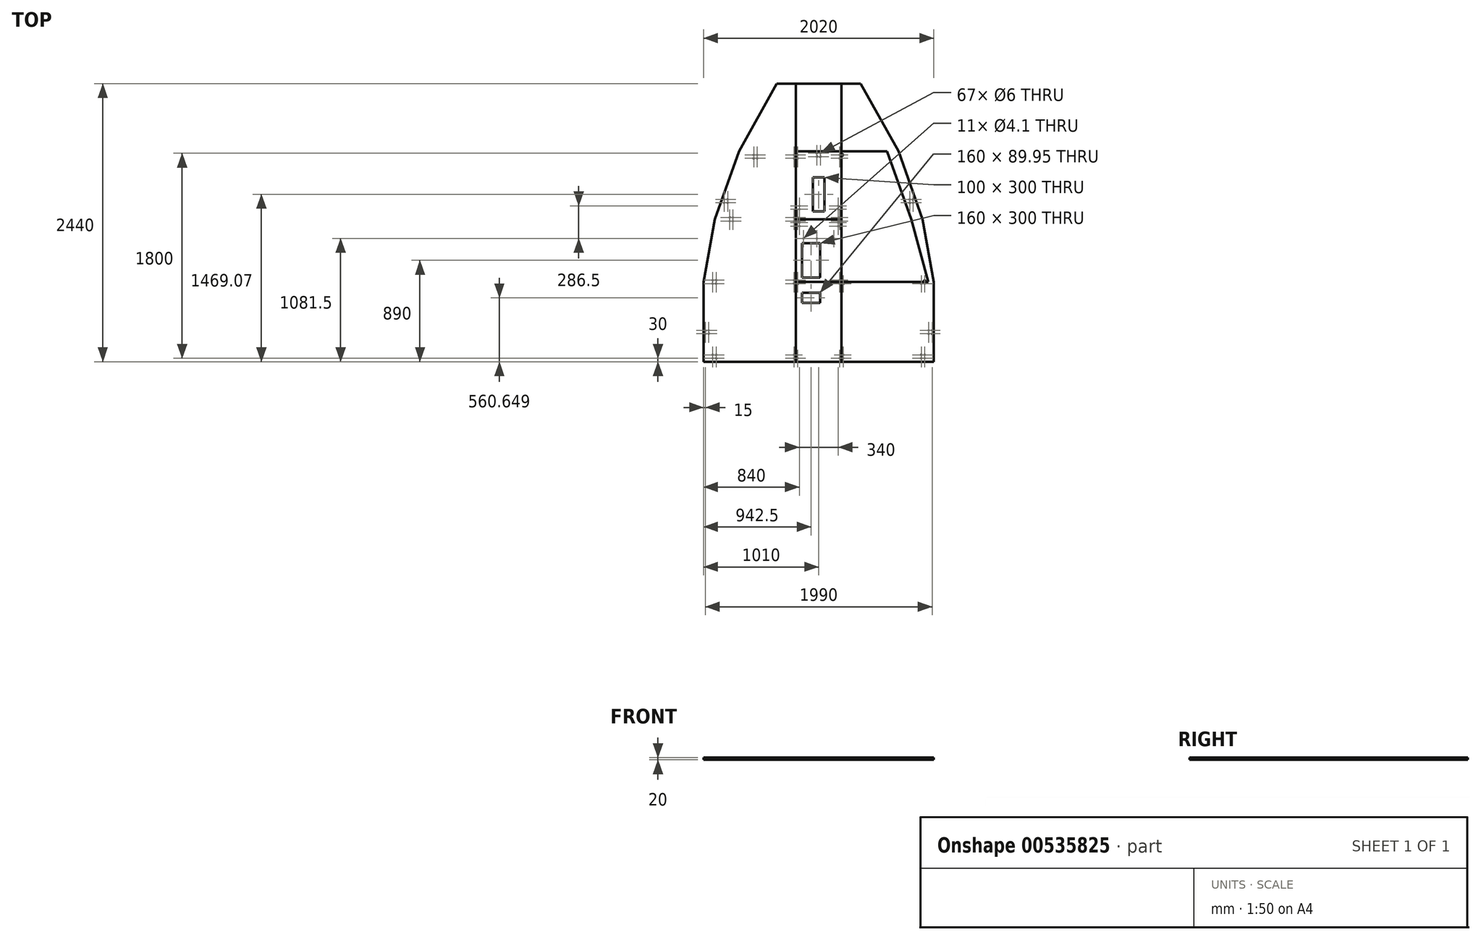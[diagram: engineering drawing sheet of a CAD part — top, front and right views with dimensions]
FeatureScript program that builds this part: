
annotation { "Feature Type Name" : "Feature", "Feature Type Description" : "" }
export const myFeature = defineFeature(function(context is Context, id is Id, definition is map)
    precondition{}
    {
        {
            var Q0;
            Q0=qCreatedBy(makeId("Top.planeOp"),FACE);
            var sketch = newSketch(context, id + "F0", { "sketchPlane" : qUnion([Q0])});
            skLineSegment(sketch, "E0.bottom", {"start": v(200, -350) * mm, "end": v(-200, -350) * mm});
            skLineSegment(sketch, "E0.top", {"start": v(200, 350) * mm, "end": v(-200, 350) * mm});
            skLineSegment(sketch, "E0.left", {"start": v(200, -350) * mm, "end": v(200, 350) * mm});
            skLineSegment(sketch, "E0.right", {"start": v(-200, -350) * mm, "end": v(-200, 350) * mm});
            skPoint(sketch, "E0.middle", {"position": v(0, 0) * mm});
            skCircle(sketch, "E1", {"center": v(185, 335) * mm, "radius": 3 * mm});
            skCircle(sketch, "E2", {"center": v(-185, 335) * mm, "radius": 3 * mm});
            skCircle(sketch, "E3", {"center": v(185, -320) * mm, "radius": 3 * mm});
            skCircle(sketch, "E4", {"center": v(-185, -320) * mm, "radius": 3 * mm});
            skLineSegment(sketch, "E5.bottom", {"start": v(12.5, 165.67) * mm, "end": v(-147.5, 165.67) * mm});
            skLineSegment(sketch, "E5.top", {"start": v(12.5, 255.63) * mm, "end": v(-147.5, 255.63) * mm});
            skLineSegment(sketch, "E5.left", {"start": v(12.5, 165.67) * mm, "end": v(12.5, 255.63) * mm});
            skLineSegment(sketch, "E5.right", {"start": v(-147.5, 165.67) * mm, "end": v(-147.5, 255.63) * mm});
            skPoint(sketch, "E5.middle", {"position": v(-67.5, 210.65) * mm});
            skSolve(sketch);
        }
        {
            var Q0;
            Q0=qSketchRegion(id+"F0",true);
            extrude(context, id + "F1", {"entities" : qUnion([Q0]), "depth" : 20 * mm});
        }
        {
            var Q0;
            Q0=qCreatedBy(makeId("Top.planeOp"),FACE);
            var sketch = newSketch(context, id + "F2", { "sketchPlane" : qUnion([Q0])});
            skLineSegment(sketch, "E6.top", {"start": v(-200, 900) * mm, "end": v(-812, 900) * mm});
            skLineSegment(sketch, "E6.left", {"start": v(-200, 350) * mm, "end": v(-200, 900) * mm});
            skPoint(sketch, "E6.middle", {"position": v(-506, 625) * mm});
            skLineSegment(sketch, "E7", {"start": v(-200, 350) * mm, "end": v(-960, 350) * mm});
            skLineSegment(sketch, "E8", {"start": v(-960, 350) * mm, "end": v(-812, 900) * mm});
            skCircle(sketch, "E9", {"center": v(-215, 885) * mm, "radius": 3 * mm});
            skCircle(sketch, "E10", {"center": v(-215, 365) * mm, "radius": 3 * mm});
            skCircle(sketch, "E11", {"center": v(-930, 365) * mm, "radius": 3 * mm});
            skCircle(sketch, "E12", {"center": v(-782, 885) * mm, "radius": 3 * mm});
            skLineSegment(sketch, "E13.left", {"start": v(-200, 900) * mm, "end": v(-200, 1495) * mm});
            skPoint(sketch, "E13.middle", {"position": v(-506, 1197.5) * mm});
            skLineSegment(sketch, "E14", {"start": v(-200, 1495) * mm, "end": v(-600, 1495) * mm});
            skLineSegment(sketch, "E15", {"start": v(-812, 900) * mm, "end": v(-600, 1495) * mm});
            skCircle(sketch, "E16", {"center": v(-215, 1465) * mm, "radius": 3 * mm});
            skCircle(sketch, "E17", {"center": v(-215, 915) * mm, "radius": 3 * mm});
            skCircle(sketch, "E18", {"center": v(-782, 915) * mm, "radius": 3 * mm});
            skCircle(sketch, "E19", {"center": v(-570, 1465) * mm, "radius": 3 * mm});
            skLineSegment(sketch, "E20", {"start": v(0, 1490.85) * mm, "end": v(0, 501.43) * mm, "construction": true});
            skCircle(sketch, "E21.MirrorC", {"center": v(215, 1465) * mm, "radius": 3 * mm});
            skCircle(sketch, "E22.MirrorC", {"center": v(930, 365) * mm, "radius": 3 * mm});
            skCircle(sketch, "E23.MirrorC", {"center": v(782, 885) * mm, "radius": 3 * mm});
            skCircle(sketch, "E24.MirrorC", {"center": v(782, 915) * mm, "radius": 3 * mm});
            skCircle(sketch, "E25.MirrorC", {"center": v(570, 1465) * mm, "radius": 3 * mm});
            skCircle(sketch, "E26.MirrorC", {"center": v(215, 885) * mm, "radius": 3 * mm});
            skCircle(sketch, "E27.MirrorC", {"center": v(215, 365) * mm, "radius": 3 * mm});
            skCircle(sketch, "E28.MirrorC", {"center": v(215, 915) * mm, "radius": 3 * mm});
            skLineSegment(sketch, "E29.MirrorCS", {"start": v(200, 1495) * mm, "end": v(600, 1495) * mm});
            skLineSegment(sketch, "E30.MirrorCS", {"start": v(960, 350) * mm, "end": v(812, 900) * mm});
            skLineSegment(sketch, "E31.MirrorCS", {"start": v(200, 900) * mm, "end": v(812, 900) * mm});
            skPoint(sketch, "E32.MirrorP", {"position": v(506, 1197.5) * mm});
            skLineSegment(sketch, "E33.MirrorCS", {"start": v(200, 350) * mm, "end": v(200, 900) * mm});
            skPoint(sketch, "E34.MirrorP", {"position": v(506, 625) * mm});
            skLineSegment(sketch, "E35.MirrorCS", {"start": v(200, 350) * mm, "end": v(960, 350) * mm});
            skLineSegment(sketch, "E36.MirrorCS", {"start": v(812, 900) * mm, "end": v(600, 1495) * mm});
            skLineSegment(sketch, "E37.MirrorCS", {"start": v(200, 900) * mm, "end": v(200, 1495) * mm});
            skCircle(sketch, "E38", {"center": v(-900, 365) * mm, "radius": 3 * mm});
            skCircle(sketch, "E39", {"center": v(-752, 885) * mm, "radius": 3 * mm});
            skCircle(sketch, "E40", {"center": v(-752, 915) * mm, "radius": 3 * mm});
            skCircle(sketch, "E41", {"center": v(-570, 1435) * mm, "radius": 3 * mm});
            skCircle(sketch, "E42", {"center": v(-540, 1465) * mm, "radius": 3 * mm});
            skCircle(sketch, "E43", {"center": v(-540, 1435) * mm, "radius": 3 * mm});
            skCircle(sketch, "E44", {"center": v(-215, 1435) * mm, "radius": 3 * mm});
            skCircle(sketch, "E45.MirrorC", {"center": v(215, 1435) * mm, "radius": 3 * mm});
            skCircle(sketch, "E46.MirrorC", {"center": v(540, 1465) * mm, "radius": 3 * mm});
            skCircle(sketch, "E47.MirrorC", {"center": v(540, 1435) * mm, "radius": 3 * mm});
            skCircle(sketch, "E48.MirrorC", {"center": v(570, 1435) * mm, "radius": 3 * mm});
            skCircle(sketch, "E49.MirrorC", {"center": v(752, 915) * mm, "radius": 3 * mm});
            skCircle(sketch, "E50.MirrorC", {"center": v(752, 885) * mm, "radius": 3 * mm});
            skCircle(sketch, "E51.MirrorC", {"center": v(900, 365) * mm, "radius": 3 * mm});
            skSolve(sketch);
        }
        {
            var Q0;
            Q0=makeQuery(id+"F2.imprint","IMPRINT",FACE,{"disambiguationData":[TD([[makeQuery(id+"F2.imprint","IMPRINT",EDGE,{"derivedFrom":sQuery(id+"F2.wireOp",EDGE,"E6.left")}),1.0]])]});
            var Q1;
            Q1=makeQuery(id+"F2.imprint","IMPRINT",FACE,{"disambiguationData":[TD([[makeQuery(id+"F2.imprint","IMPRINT",EDGE,{"derivedFrom":sQuery(id+"F2.wireOp",EDGE,"E22.MirrorC")}),1.0]])]});
            extrude(context, id + "F3", {"entities" : qUnion([Q0, Q1]), "depth" : 20 * mm});
        }
        {
            var Q0;
            Q0=makeQuery(id+"F2.imprint","IMPRINT",FACE,{"disambiguationData":[TD([[makeQuery(id+"F2.imprint","IMPRINT",EDGE,{"derivedFrom":sQuery(id+"F2.wireOp",EDGE,"E6.top")}),-1.0]])]});
            var Q1;
            Q1=makeQuery(id+"F2.imprint","IMPRINT",FACE,{"disambiguationData":[TD([[makeQuery(id+"F2.imprint","IMPRINT",EDGE,{"derivedFrom":sQuery(id+"F2.wireOp",EDGE,"E21.MirrorC")}),1.0]])]});
            extrude(context, id + "F4", {"entities" : qUnion([Q0, Q1]), "depth" : 20 * mm});
        }
        {
            var Q0;
            Q0=qCreatedBy(makeId("Top.planeOp"),FACE);
            var sketch = newSketch(context, id + "F5", { "sketchPlane" : qUnion([Q0])});
            skLineSegment(sketch, "E52.bottom", {"start": v(200, 900) * mm, "end": v(-200, 900) * mm});
            skLineSegment(sketch, "E52.top", {"start": v(200, 350) * mm, "end": v(-200, 350) * mm});
            skLineSegment(sketch, "E52.left", {"start": v(200, 900) * mm, "end": v(200, 350) * mm});
            skLineSegment(sketch, "E52.right", {"start": v(-200, 900) * mm, "end": v(-200, 350) * mm});
            skPoint(sketch, "E52.middle", {"position": v(0, 625) * mm});
            skCircle(sketch, "E53", {"center": v(-132.5, 731.5) * mm, "radius": 2.05 * mm});
            skCircle(sketch, "E54", {"center": v(-17.5, 731.5) * mm, "radius": 2.05 * mm});
            skCircle(sketch, "E55", {"center": v(132.5, 731.5) * mm, "radius": 2.05 * mm});
            skCircle(sketch, "E56", {"center": v(-185, 885) * mm, "radius": 3 * mm});
            skCircle(sketch, "E57", {"center": v(185, 885) * mm, "radius": 3 * mm});
            skCircle(sketch, "E58", {"center": v(-185, 365) * mm, "radius": 3 * mm});
            skCircle(sketch, "E59", {"center": v(185, 365) * mm, "radius": 3 * mm});
            skCircle(sketch, "E60", {"center": v(170, 870) * mm, "radius": 2.05 * mm});
            skCircle(sketch, "E61", {"center": v(170, 840) * mm, "radius": 2.05 * mm});
            skLineSegment(sketch, "E62", {"start": v(0, 625) * mm, "end": v(0, 499.57) * mm, "construction": true});
            skCircle(sketch, "E63.MirrorC", {"center": v(-170, 840) * mm, "radius": 2.05 * mm});
            skCircle(sketch, "E64.MirrorC", {"center": v(-170, 870) * mm, "radius": 2.05 * mm});
            skLineSegment(sketch, "E65.bottom", {"start": v(12.5, 390) * mm, "end": v(-147.5, 390) * mm});
            skLineSegment(sketch, "E65.top", {"start": v(12.5, 690) * mm, "end": v(-147.5, 690) * mm});
            skLineSegment(sketch, "E65.left", {"start": v(12.5, 390) * mm, "end": v(12.5, 690) * mm});
            skLineSegment(sketch, "E65.right", {"start": v(-147.5, 390) * mm, "end": v(-147.5, 690) * mm});
            skPoint(sketch, "E65.middle", {"position": v(-67.5, 540) * mm});
            skSolve(sketch);
        }
        {
            var Q0;
            Q0=qSketchRegion(id+"F5",true);
            extrude(context, id + "F6", {"entities" : qUnion([Q0]), "depth" : 20 * mm});
        }
        {
            var Q0;
            Q0=qCreatedBy(makeId("Top.planeOp"),FACE);
            var sketch = newSketch(context, id + "F7", { "sketchPlane" : qUnion([Q0])});
            skLineSegment(sketch, "E66.bottom", {"start": v(-200, 900) * mm, "end": v(200, 900) * mm});
            skLineSegment(sketch, "E66.top", {"start": v(200, 1495) * mm, "end": v(-200, 1495) * mm});
            skLineSegment(sketch, "E66.left", {"start": v(-200, 900) * mm, "end": v(-200, 1495) * mm});
            skLineSegment(sketch, "E66.right", {"start": v(200, 900) * mm, "end": v(200, 1495) * mm});
            skPoint(sketch, "E66.middle", {"position": v(0, 1197.5) * mm});
            skCircle(sketch, "E67", {"center": v(170, 970) * mm, "radius": 2.05 * mm, "construction": true});
            skCircle(sketch, "E68", {"center": v(170, 940) * mm, "radius": 2.05 * mm, "construction": true});
            skCircle(sketch, "E69", {"center": v(170, 988) * mm, "radius": 2.05 * mm});
            skCircle(sketch, "E70", {"center": v(170, 1018) * mm, "radius": 2.05 * mm});
            skCircle(sketch, "E71.MirrorC", {"center": v(-170, 970) * mm, "radius": 2.05 * mm, "construction": true});
            skCircle(sketch, "E72.MirrorC", {"center": v(-170, 988) * mm, "radius": 2.05 * mm});
            skCircle(sketch, "E73.MirrorC", {"center": v(-170, 1018) * mm, "radius": 2.05 * mm});
            skCircle(sketch, "E74.MirrorC", {"center": v(-170, 940) * mm, "radius": 2.05 * mm, "construction": true});
            skCircle(sketch, "E75", {"center": v(185, 1465) * mm, "radius": 3 * mm});
            skCircle(sketch, "E76", {"center": v(-185, 1465) * mm, "radius": 3 * mm});
            skCircle(sketch, "E77", {"center": v(185, 915) * mm, "radius": 3 * mm});
            skCircle(sketch, "E78", {"center": v(-185, 915) * mm, "radius": 3 * mm});
            skCircle(sketch, "E79", {"center": v(-185, 1435) * mm, "radius": 3 * mm});
            skCircle(sketch, "E80", {"center": v(185, 1435) * mm, "radius": 3 * mm});
            skLineSegment(sketch, "E81.bottom", {"start": v(50, 969.07) * mm, "end": v(-50, 969.07) * mm});
            skLineSegment(sketch, "E81.top", {"start": v(50, 1269.07) * mm, "end": v(-50, 1269.07) * mm});
            skLineSegment(sketch, "E81.left", {"start": v(50, 969.07) * mm, "end": v(50, 1269.07) * mm});
            skLineSegment(sketch, "E81.right", {"start": v(-50, 969.07) * mm, "end": v(-50, 1269.07) * mm});
            skPoint(sketch, "E81.middle", {"position": v(0, 1119.07) * mm});
            skCircle(sketch, "E82", {"center": v(15, 1450) * mm, "radius": 3 * mm});
            skCircle(sketch, "E83", {"center": v(-15, 1450) * mm, "radius": 3 * mm});
            skCircle(sketch, "E84", {"center": v(15, 1480) * mm, "radius": 3 * mm});
            skCircle(sketch, "E85", {"center": v(-15, 1480) * mm, "radius": 3 * mm});
            skSolve(sketch);
        }
        {
            var Q0;
            Q0=qSketchRegion(id+"F7",true);
            extrude(context, id + "F8", {"entities" : qUnion([Q0]), "depth" : 20 * mm});
        }
        {
            var Q0;
            Q0=qCreatedBy(makeId("Top.planeOp"),FACE);
            var sketch = newSketch(context, id + "F9", { "sketchPlane" : qUnion([Q0])});
            skLineSegment(sketch, "E86.bottom", {"start": v(-200, -350) * mm, "end": v(-960, -350) * mm});
            skLineSegment(sketch, "E86.top", {"start": v(-200, 350) * mm, "end": v(-960, 350) * mm});
            skLineSegment(sketch, "E86.left", {"start": v(-200, -350) * mm, "end": v(-200, 350) * mm});
            skLineSegment(sketch, "E86.right", {"start": v(-960, -350) * mm, "end": v(-960, 350) * mm});
            skPoint(sketch, "E86.middle", {"position": v(-580, 0) * mm});
            skPoint(sketch, "E87", {"position": v(-930, 335) * mm});
            skPoint(sketch, "E88", {"position": v(-215, 335) * mm});
            skPoint(sketch, "E89", {"position": v(-930, -320) * mm});
            skPoint(sketch, "E90", {"position": v(-215, -320) * mm});
            skCircle(sketch, "E91", {"center": v(-930, 335) * mm, "radius": 3 * mm});
            skCircle(sketch, "E92", {"center": v(-215, 335) * mm, "radius": 3 * mm});
            skCircle(sketch, "E93", {"center": v(-930, -320) * mm, "radius": 3 * mm});
            skCircle(sketch, "E94", {"center": v(-215, -320) * mm, "radius": 3 * mm});
            skLineSegment(sketch, "E95.bottom", {"start": v(200, -350) * mm, "end": v(960, -350) * mm});
            skLineSegment(sketch, "E95.top", {"start": v(200, 350) * mm, "end": v(960, 350) * mm});
            skLineSegment(sketch, "E95.left", {"start": v(200, -350) * mm, "end": v(200, 350) * mm});
            skLineSegment(sketch, "E95.right", {"start": v(960, -350) * mm, "end": v(960, 350) * mm});
            skPoint(sketch, "E95.middle", {"position": v(580, 0) * mm});
            skCircle(sketch, "E96", {"center": v(215, 335) * mm, "radius": 3 * mm});
            skCircle(sketch, "E97", {"center": v(930, 335) * mm, "radius": 3 * mm});
            skCircle(sketch, "E98", {"center": v(215, -320) * mm, "radius": 3 * mm});
            skCircle(sketch, "E99", {"center": v(930, -320) * mm, "radius": 3 * mm});
            skCircle(sketch, "E100", {"center": v(-930, -290) * mm, "radius": 3 * mm});
            skCircle(sketch, "E101", {"center": v(-900, -320) * mm, "radius": 3 * mm});
            skCircle(sketch, "E102", {"center": v(-900, -290) * mm, "radius": 3 * mm});
            skCircle(sketch, "E103", {"center": v(-215, -290) * mm, "radius": 3 * mm});
            skCircle(sketch, "E104", {"center": v(-900, 335) * mm, "radius": 3 * mm});
            skCircle(sketch, "E105", {"center": v(900, -320) * mm, "radius": 3 * mm});
            skCircle(sketch, "E106", {"center": v(930, -290) * mm, "radius": 3 * mm});
            skCircle(sketch, "E107", {"center": v(900, -290) * mm, "radius": 3 * mm});
            skCircle(sketch, "E108", {"center": v(215, -290) * mm, "radius": 3 * mm});
            skCircle(sketch, "E109", {"center": v(900, 335) * mm, "radius": 3 * mm});
            skSolve(sketch);
        }
        {
            var Q0;
            Q0=qSketchRegion(id+"F9",true);
            extrude(context, id + "F10", {"entities" : qUnion([Q0]), "depth" : 20 * mm});
        }
        {
            var Q0;
            Q0=makeQuery(id+"F8.opExtrude","CAP_FACE",FACE,{"disambiguationData":[OSD([sQuery(id+"F7.wireOp",EDGE,"E66.bottom"),sQuery(id+"F7.wireOp",EDGE,"E66.top"),sQuery(id+"F7.wireOp",EDGE,"E66.left"),sQuery(id+"F7.wireOp",EDGE,"E66.right"),sQuery(id+"F7.wireOp",EDGE,"E69"),sQuery(id+"F7.wireOp",EDGE,"E70"),sQuery(id+"F7.wireOp",EDGE,"E72.MirrorC"),sQuery(id+"F7.wireOp",EDGE,"E73.MirrorC"),sQuery(id+"F7.wireOp",EDGE,"E75"),sQuery(id+"F7.wireOp",EDGE,"E76"),sQuery(id+"F7.wireOp",EDGE,"E77"),sQuery(id+"F7.wireOp",EDGE,"E78"),sQuery(id+"F7.wireOp",EDGE,"E79"),sQuery(id+"F7.wireOp",EDGE,"E80"),sQuery(id+"F7.wireOp",EDGE,"E81.bottom"),sQuery(id+"F7.wireOp",EDGE,"E81.top"),sQuery(id+"F7.wireOp",EDGE,"E81.left"),sQuery(id+"F7.wireOp",EDGE,"E81.right")])],"isStart":false});
            var sketch = newSketch(context, id + "F11", { "sketchPlane" : qUnion([Q0])});
            skLineSegment(sketch, "E110.bottom", {"start": v(-200, 1495) * mm, "end": v(200, 1495) * mm});
            skLineSegment(sketch, "E110.top", {"start": v(-200, 2090) * mm, "end": v(200, 2090) * mm});
            skLineSegment(sketch, "E110.left", {"start": v(-200, 1495) * mm, "end": v(-200, 2090) * mm});
            skLineSegment(sketch, "E110.right", {"start": v(200, 1495) * mm, "end": v(200, 2090) * mm});
            skSolve(sketch);
        }
        {
            var Q0;
            Q0 = qSketchRegion(id + "F11", true);
            extrude(context, id + "F12", {"entities" : qUnion([Q0]), "oppositeDirection" : true, "depth" : 20 * mm, "offsetDistance" : 25 * mm});
        }
        {
            var Q0;
            Q0=makeQuery(id+"F8.opExtrude","CAP_FACE",FACE,{"disambiguationData":[OSD([sQuery(id+"F7.wireOp",EDGE,"E66.bottom"),sQuery(id+"F7.wireOp",EDGE,"E66.top"),sQuery(id+"F7.wireOp",EDGE,"E66.left"),sQuery(id+"F7.wireOp",EDGE,"E66.right"),sQuery(id+"F7.wireOp",EDGE,"E69"),sQuery(id+"F7.wireOp",EDGE,"E70"),sQuery(id+"F7.wireOp",EDGE,"E72.MirrorC"),sQuery(id+"F7.wireOp",EDGE,"E73.MirrorC"),sQuery(id+"F7.wireOp",EDGE,"E75"),sQuery(id+"F7.wireOp",EDGE,"E76"),sQuery(id+"F7.wireOp",EDGE,"E77"),sQuery(id+"F7.wireOp",EDGE,"E78"),sQuery(id+"F7.wireOp",EDGE,"E79"),sQuery(id+"F7.wireOp",EDGE,"E80"),sQuery(id+"F7.wireOp",EDGE,"E81.bottom"),sQuery(id+"F7.wireOp",EDGE,"E81.top"),sQuery(id+"F7.wireOp",EDGE,"E81.left"),sQuery(id+"F7.wireOp",EDGE,"E81.right")])],"isStart":false});
            var sketch = newSketch(context, id + "F13", { "sketchPlane" : qUnion([Q0])});
            skLineSegment(sketch, "E111", {"start": v(-200, 1495) * mm, "end": v(-600, 1495) * mm});
            skLineSegment(sketch, "E112", {"start": v(-600, 1495) * mm, "end": v(-268, 2090) * mm});
            skLineSegment(sketch, "E113", {"start": v(-268, 2090) * mm, "end": v(-200, 2090) * mm});
            skLineSegment(sketch, "E114", {"start": v(-200, 2090) * mm, "end": v(-200, 1495) * mm});
            skSolve(sketch);
        }
        {
            var Q0;
            Q0=makeQuery(id+"F13.imprint","IMPRINT",FACE,{"disambiguationData":[TD([[makeQuery(id+"F13.imprint","IMPRINT",EDGE,{"derivedFrom":sQuery(id+"F13.wireOp",EDGE,"E111")}),-1.0]])]});
            extrude(context, id + "F14", {"entities" : qUnion([Q0]), "oppositeDirection" : true, "depth" : 20 * mm, "offsetDistance" : 25 * mm});
        }
        {
            var Q0;
            Q0=makeQuery(id+"F8.opExtrude","CAP_FACE",FACE,{"disambiguationData":[OSD([sQuery(id+"F7.wireOp",EDGE,"E66.bottom"),sQuery(id+"F7.wireOp",EDGE,"E66.top"),sQuery(id+"F7.wireOp",EDGE,"E66.left"),sQuery(id+"F7.wireOp",EDGE,"E66.right"),sQuery(id+"F7.wireOp",EDGE,"E69"),sQuery(id+"F7.wireOp",EDGE,"E70"),sQuery(id+"F7.wireOp",EDGE,"E72.MirrorC"),sQuery(id+"F7.wireOp",EDGE,"E73.MirrorC"),sQuery(id+"F7.wireOp",EDGE,"E75"),sQuery(id+"F7.wireOp",EDGE,"E76"),sQuery(id+"F7.wireOp",EDGE,"E77"),sQuery(id+"F7.wireOp",EDGE,"E78"),sQuery(id+"F7.wireOp",EDGE,"E79"),sQuery(id+"F7.wireOp",EDGE,"E80"),sQuery(id+"F7.wireOp",EDGE,"E81.bottom"),sQuery(id+"F7.wireOp",EDGE,"E81.top"),sQuery(id+"F7.wireOp",EDGE,"E81.left"),sQuery(id+"F7.wireOp",EDGE,"E81.right")])],"isStart":false});
            var sketch = newSketch(context, id + "F15", { "sketchPlane" : qUnion([Q0])});
            skLineSegment(sketch, "E115", {"start": v(200, 1495) * mm, "end": v(600, 1495) * mm});
            skLineSegment(sketch, "E116", {"start": v(600, 1495) * mm, "end": v(268, 2090) * mm});
            skLineSegment(sketch, "E117", {"start": v(268, 2090) * mm, "end": v(200, 2090) * mm});
            skLineSegment(sketch, "E118", {"start": v(200, 2090) * mm, "end": v(200, 1495) * mm});
            skSolve(sketch);
        }
        {
            var Q0;
            Q0 = qSketchRegion(id + "F15", true);
            extrude(context, id + "F16", {"entities" : qUnion([Q0]), "oppositeDirection" : true, "depth" : 20 * mm, "offsetDistance" : 25 * mm});
        }
        {
            var Q0;
            Q0=makeQuery(id+"F10.opExtrude","CAP_FACE",FACE,{"disambiguationData":[OSD([sQuery(id+"F9.wireOp",EDGE,"E86.bottom"),sQuery(id+"F9.wireOp",EDGE,"E86.top"),sQuery(id+"F9.wireOp",EDGE,"E86.left"),sQuery(id+"F9.wireOp",EDGE,"E86.right"),sQuery(id+"F9.wireOp",EDGE,"E91"),sQuery(id+"F9.wireOp",EDGE,"E92"),sQuery(id+"F9.wireOp",EDGE,"E93"),sQuery(id+"F9.wireOp",EDGE,"E94"),sQuery(id+"F9.wireOp",EDGE,"E100"),sQuery(id+"F9.wireOp",EDGE,"E101"),sQuery(id+"F9.wireOp",EDGE,"E102"),sQuery(id+"F9.wireOp",EDGE,"E103"),sQuery(id+"F9.wireOp",EDGE,"E104")])],"isStart":true});
            var sketch = newSketch(context, id + "F17", { "sketchPlane" : qUnion([Q0])});
            skLineSegment(sketch, "E119.bottom", {"start": v(-960, -350) * mm, "end": v(-1010, -350) * mm});
            skLineSegment(sketch, "E119.top", {"start": v(-960, 350) * mm, "end": v(-1010, 350) * mm});
            skLineSegment(sketch, "E119.left", {"start": v(-960, -350) * mm, "end": v(-960, 350) * mm});
            skLineSegment(sketch, "E119.right", {"start": v(-1010, -350) * mm, "end": v(-1010, 350) * mm});
            skCircle(sketch, "E120", {"center": v(-965, 75) * mm, "radius": 3 * mm});
            skCircle(sketch, "E121", {"center": v(-995, 75) * mm, "radius": 3 * mm});
            skCircle(sketch, "E122", {"center": v(-965, 105) * mm, "radius": 3 * mm});
            skCircle(sketch, "E123", {"center": v(-995, 105) * mm, "radius": 3 * mm});
            skSolve(sketch);
        }
        {
            var Q0;
            Q0=makeQuery(id+"F10.opExtrude","CAP_FACE",FACE,{"disambiguationData":[OSD([sQuery(id+"F9.wireOp",EDGE,"E95.bottom"),sQuery(id+"F9.wireOp",EDGE,"E95.top"),sQuery(id+"F9.wireOp",EDGE,"E95.left"),sQuery(id+"F9.wireOp",EDGE,"E95.right"),sQuery(id+"F9.wireOp",EDGE,"E96"),sQuery(id+"F9.wireOp",EDGE,"E97"),sQuery(id+"F9.wireOp",EDGE,"E98"),sQuery(id+"F9.wireOp",EDGE,"E99"),sQuery(id+"F9.wireOp",EDGE,"E105"),sQuery(id+"F9.wireOp",EDGE,"E106"),sQuery(id+"F9.wireOp",EDGE,"E107"),sQuery(id+"F9.wireOp",EDGE,"E108"),sQuery(id+"F9.wireOp",EDGE,"E109")])],"isStart":true});
            var sketch = newSketch(context, id + "F18", { "sketchPlane" : qUnion([Q0])});
            skLineSegment(sketch, "E124.bottom", {"start": v(960, 350) * mm, "end": v(1010, 350) * mm});
            skLineSegment(sketch, "E124.top", {"start": v(960, -350) * mm, "end": v(1010, -350) * mm});
            skLineSegment(sketch, "E124.left", {"start": v(960, 350) * mm, "end": v(960, -350) * mm});
            skLineSegment(sketch, "E124.right", {"start": v(1010, 350) * mm, "end": v(1010, -350) * mm});
            skCircle(sketch, "E125", {"center": v(995, 75) * mm, "radius": 3 * mm});
            skCircle(sketch, "E126", {"center": v(965, 75) * mm, "radius": 3 * mm});
            skCircle(sketch, "E127", {"center": v(995, 105) * mm, "radius": 3 * mm});
            skCircle(sketch, "E128", {"center": v(965, 105) * mm, "radius": 3 * mm});
            skSolve(sketch);
        }
        {
            var Q0;
            Q0 = qSketchRegion(id + "F17", true);
            extrude(context, id + "F19", {"entities" : qUnion([Q0]), "operationType" : NewBodyOperationType.ADD, "oppositeDirection" : true, "depth" : 20 * mm, "offsetDistance" : 25 * mm});
        }
        {
            var Q0;
            Q0 = qSketchRegion(id + "F18", true);
            extrude(context, id + "F20", {"entities" : qUnion([Q0]), "operationType" : NewBodyOperationType.ADD, "oppositeDirection" : true, "depth" : 20 * mm, "offsetDistance" : 25 * mm});
        }
        {
            var Q0;
            Q0=makeQuery(id+"F4.opExtrude","CAP_FACE",FACE,{"disambiguationData":[OSD([sQuery(id+"F2.wireOp",EDGE,"E6.top"),sQuery(id+"F2.wireOp",EDGE,"E13.left"),sQuery(id+"F2.wireOp",EDGE,"E14"),sQuery(id+"F2.wireOp",EDGE,"E15"),sQuery(id+"F2.wireOp",EDGE,"E16"),sQuery(id+"F2.wireOp",EDGE,"E17"),sQuery(id+"F2.wireOp",EDGE,"E18"),sQuery(id+"F2.wireOp",EDGE,"E19"),sQuery(id+"F2.wireOp",EDGE,"E40"),sQuery(id+"F2.wireOp",EDGE,"E41"),sQuery(id+"F2.wireOp",EDGE,"E42"),sQuery(id+"F2.wireOp",EDGE,"E43"),sQuery(id+"F2.wireOp",EDGE,"E44")])],"isStart":true});
            var sketch = newSketch(context, id + "F21", { "sketchPlane" : qUnion([Q0])});
            skLineSegment(sketch, "E129", {"start": v(-600, -1495) * mm, "end": v(-812, -900) * mm});
            skLineSegment(sketch, "E130", {"start": v(-812, -900) * mm, "end": v(-912, -900) * mm});
            skLineSegment(sketch, "E131", {"start": v(-912, -900) * mm, "end": v(-700, -1495) * mm});
            skLineSegment(sketch, "E132", {"start": v(-700, -1495) * mm, "end": v(-600, -1495) * mm});
            skCircle(sketch, "E133", {"center": v(-798.42, -1075) * mm, "radius": 3 * mm});
            skCircle(sketch, "E134", {"center": v(-828.42, -1075) * mm, "radius": 3 * mm});
            skCircle(sketch, "E135", {"center": v(-798.42, -1045) * mm, "radius": 3 * mm});
            skCircle(sketch, "E136", {"center": v(-828.42, -1045) * mm, "radius": 3 * mm});
            skSolve(sketch);
        }
        {
            var Q0;
            Q0=makeQuery(id+"F4.opExtrude","CAP_FACE",FACE,{"disambiguationData":[OSD([sQuery(id+"F2.wireOp",EDGE,"E21.MirrorC"),sQuery(id+"F2.wireOp",EDGE,"E24.MirrorC"),sQuery(id+"F2.wireOp",EDGE,"E25.MirrorC"),sQuery(id+"F2.wireOp",EDGE,"E28.MirrorC"),sQuery(id+"F2.wireOp",EDGE,"E29.MirrorCS"),sQuery(id+"F2.wireOp",EDGE,"E31.MirrorCS"),sQuery(id+"F2.wireOp",EDGE,"E36.MirrorCS"),sQuery(id+"F2.wireOp",EDGE,"E37.MirrorCS"),sQuery(id+"F2.wireOp",EDGE,"E45.MirrorC"),sQuery(id+"F2.wireOp",EDGE,"E46.MirrorC"),sQuery(id+"F2.wireOp",EDGE,"E47.MirrorC"),sQuery(id+"F2.wireOp",EDGE,"E48.MirrorC"),sQuery(id+"F2.wireOp",EDGE,"E49.MirrorC")])],"isStart":true});
            var sketch = newSketch(context, id + "F22", { "sketchPlane" : qUnion([Q0])});
            skLineSegment(sketch, "E137", {"start": v(812, -900) * mm, "end": v(600, -1495) * mm});
            skLineSegment(sketch, "E138", {"start": v(600, -1495) * mm, "end": v(700, -1495) * mm});
            skLineSegment(sketch, "E139", {"start": v(700, -1495) * mm, "end": v(912, -900) * mm});
            skLineSegment(sketch, "E140", {"start": v(912, -900) * mm, "end": v(812, -900) * mm});
            skCircle(sketch, "E141", {"center": v(828.42, -1075) * mm, "radius": 3 * mm});
            skCircle(sketch, "E142", {"center": v(798.42, -1075) * mm, "radius": 3 * mm});
            skCircle(sketch, "E143", {"center": v(828.42, -1045) * mm, "radius": 3 * mm});
            skCircle(sketch, "E144", {"center": v(798.42, -1045) * mm, "radius": 3 * mm});
            skSolve(sketch);
        }
        {
            var Q0;
            Q0 = qSketchRegion(id + "F21", true);
            extrude(context, id + "F23", {"entities" : qUnion([Q0]), "operationType" : NewBodyOperationType.ADD, "oppositeDirection" : true, "depth" : 20 * mm, "offsetDistance" : 25 * mm});
        }
        {
            var Q0;
            Q0 = qSketchRegion(id + "F22", true);
            extrude(context, id + "F24", {"entities" : qUnion([Q0]), "operationType" : NewBodyOperationType.ADD, "oppositeDirection" : true, "depth" : 20 * mm, "offsetDistance" : 25 * mm});
        }
        {
            var Q0;
            Q0=makeQuery(id+"F3.opExtrude","CAP_FACE",FACE,{"disambiguationData":[OSD([sQuery(id+"F2.wireOp",EDGE,"E6.left"),sQuery(id+"F2.wireOp",EDGE,"E7"),sQuery(id+"F2.wireOp",EDGE,"E8"),sQuery(id+"F2.wireOp",EDGE,"E9"),sQuery(id+"F2.wireOp",EDGE,"E10"),sQuery(id+"F2.wireOp",EDGE,"E11"),sQuery(id+"F2.wireOp",EDGE,"E12"),sQuery(id+"F2.wireOp",EDGE,"E6.top"),sQuery(id+"F2.wireOp",EDGE,"E38"),sQuery(id+"F2.wireOp",EDGE,"E39")])],"isStart":true});
            var sketch = newSketch(context, id + "F25", { "sketchPlane" : qUnion([Q0])});
            skLineSegment(sketch, "E145", {"start": v(-812, -900) * mm, "end": v(-912, -900) * mm});
            skLineSegment(sketch, "E146", {"start": v(-912, -900) * mm, "end": v(-1010, -350) * mm});
            skLineSegment(sketch, "E147", {"start": v(-1010, -350) * mm, "end": v(-960, -350) * mm});
            skLineSegment(sketch, "E148", {"start": v(-960, -350) * mm, "end": v(-812, -900) * mm});
            skSolve(sketch);
        }
        {
            var Q0;
            Q0 = qSketchRegion(id + "F25", true);
            extrude(context, id + "F26", {"entities" : qUnion([Q0]), "operationType" : NewBodyOperationType.ADD, "oppositeDirection" : true, "depth" : 20 * mm, "offsetDistance" : 25 * mm});
        }
        {
            var Q0;
            Q0=makeQuery(id+"F3.opExtrude","CAP_FACE",FACE,{"disambiguationData":[OSD([sQuery(id+"F2.wireOp",EDGE,"E22.MirrorC"),sQuery(id+"F2.wireOp",EDGE,"E23.MirrorC"),sQuery(id+"F2.wireOp",EDGE,"E26.MirrorC"),sQuery(id+"F2.wireOp",EDGE,"E27.MirrorC"),sQuery(id+"F2.wireOp",EDGE,"E30.MirrorCS"),sQuery(id+"F2.wireOp",EDGE,"E33.MirrorCS"),sQuery(id+"F2.wireOp",EDGE,"E31.MirrorCS"),sQuery(id+"F2.wireOp",EDGE,"E35.MirrorCS"),sQuery(id+"F2.wireOp",EDGE,"E50.MirrorC"),sQuery(id+"F2.wireOp",EDGE,"E51.MirrorC")])],"isStart":true});
            var sketch = newSketch(context, id + "F27", { "sketchPlane" : qUnion([Q0])});
            skLineSegment(sketch, "E149", {"start": v(960, -350) * mm, "end": v(812, -900) * mm});
            skLineSegment(sketch, "E150", {"start": v(812, -900) * mm, "end": v(912, -900) * mm});
            skLineSegment(sketch, "E151", {"start": v(912, -900) * mm, "end": v(1010, -350) * mm});
            skLineSegment(sketch, "E152", {"start": v(1010, -350) * mm, "end": v(960, -350) * mm});
            skSolve(sketch);
        }
        {
            var Q0;
            Q0 = qSketchRegion(id + "F27", true);
            extrude(context, id + "F28", {"entities" : qUnion([Q0]), "operationType" : NewBodyOperationType.ADD, "oppositeDirection" : true, "depth" : 20 * mm, "offsetDistance" : 25 * mm});
        }
        {
            var Q0;
            Q0=makeQuery(id+"F16.opExtrude","CAP_FACE",FACE,{"disambiguationData":[OSD([sQuery(id+"F15.wireOp",EDGE,"E115"),sQuery(id+"F15.wireOp",EDGE,"E116"),sQuery(id+"F15.wireOp",EDGE,"E117"),sQuery(id+"F15.wireOp",EDGE,"E118")])],"isStart":false});
            var sketch = newSketch(context, id + "F29", { "sketchPlane" : qUnion([Q0])});
            skLineSegment(sketch, "E153", {"start": v(600, -1495) * mm, "end": v(268, -2090) * mm});
            skLineSegment(sketch, "E154", {"start": v(268, -2090) * mm, "end": v(368, -2090) * mm});
            skLineSegment(sketch, "E155", {"start": v(368, -2090) * mm, "end": v(700, -1495) * mm});
            skLineSegment(sketch, "E156", {"start": v(700, -1495) * mm, "end": v(600, -1495) * mm});
            skSolve(sketch);
        }
        {
            var Q0;
            Q0 = qSketchRegion(id + "F29", true);
            extrude(context, id + "F30", {"entities" : qUnion([Q0]), "operationType" : NewBodyOperationType.ADD, "oppositeDirection" : true, "depth" : 20 * mm, "offsetDistance" : 25 * mm});
        }
        {
            var Q0;
            Q0=makeQuery(id+"F14.opExtrude","CAP_FACE",FACE,{"disambiguationData":[OSD([sQuery(id+"F13.wireOp",EDGE,"E111"),sQuery(id+"F13.wireOp",EDGE,"E112"),sQuery(id+"F13.wireOp",EDGE,"E113"),sQuery(id+"F13.wireOp",EDGE,"E114")])],"isStart":false});
            var sketch = newSketch(context, id + "F31", { "sketchPlane" : qUnion([Q0])});
            skLineSegment(sketch, "E157", {"start": v(-600, -1495) * mm, "end": v(-268, -2090) * mm});
            skLineSegment(sketch, "E158", {"start": v(-268, -2090) * mm, "end": v(-368, -2090) * mm});
            skLineSegment(sketch, "E159", {"start": v(-368, -2090) * mm, "end": v(-700, -1495) * mm});
            skLineSegment(sketch, "E160", {"start": v(-700, -1495) * mm, "end": v(-600, -1495) * mm});
            skSolve(sketch);
        }
        {
            var Q0;
            Q0 = qSketchRegion(id + "F31", true);
            extrude(context, id + "F32", {"entities" : qUnion([Q0]), "operationType" : NewBodyOperationType.ADD, "oppositeDirection" : true, "depth" : 20 * mm, "offsetDistance" : 25 * mm});
        }
    });
